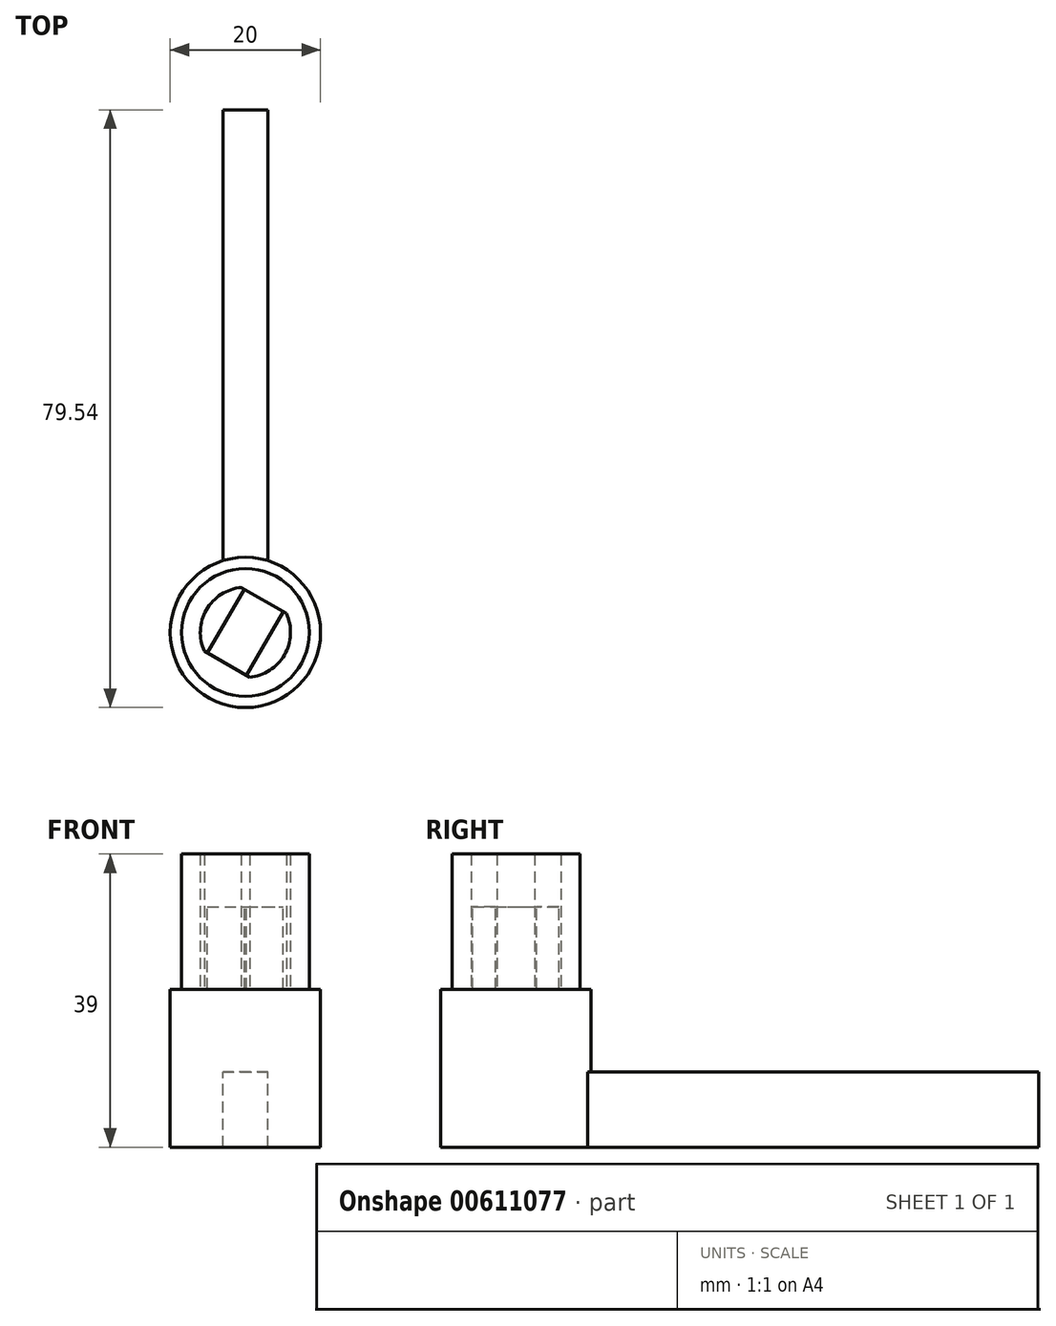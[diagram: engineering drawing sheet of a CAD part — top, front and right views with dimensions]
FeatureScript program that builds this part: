
annotation { "Feature Type Name" : "Feature", "Feature Type Description" : "" }
export const myFeature = defineFeature(function(context is Context, id is Id, definition is map)
    precondition{}
    {
        {
            var Q0;
            Q0=qCreatedBy(makeId("Top.planeOp"),FACE);
            var sketch = newSketch(context, id + "F0", { "sketchPlane" : qUnion([Q0])});
            skCircle(sketch, "E0", {"center": v(0, 0) * mm, "radius": 8.5 * mm});
            skArc(sketch, "E1", {"start": v(-0.55, 5.97) * mm, "mid": v(-5.2, 3) * mm, "end": v(-5.45, -2.51) * mm});
            skLineSegment(sketch, "E2.bottom", {"start": v(-0.55, 5.97) * mm, "end": v(5.45, 2.51) * mm});
            skLineSegment(sketch, "E2.top", {"start": v(-5.45, -2.51) * mm, "end": v(0.55, -5.97) * mm});
            skLineSegment(sketch, "E2.left", {"start": v(-0.55, 5.97) * mm, "end": v(-5.45, -2.51) * mm, "construction": true});
            skLineSegment(sketch, "E2.right", {"start": v(5.45, 2.51) * mm, "end": v(0.55, -5.97) * mm, "construction": true});
            skLineSegment(sketch, "E3", {"start": v(0, 0) * mm, "end": v(0, -6) * mm, "construction": true});
            skArc(sketch, "E4.trimOffspring", {"start": v(0.55, -5.97) * mm, "mid": v(5.2, -3) * mm, "end": v(5.45, 2.51) * mm});
            skSolve(sketch);
        }
        {
            var Q0;
            Q0=makeQuery(id+"F0.imprint","IMPRINT",FACE,{"disambiguationData":[TD([[makeQuery(id+"F0.imprint","IMPRINT",EDGE,{"derivedFrom":sQuery(id+"F0.wireOp",EDGE,"E0")}),1.0]])]});
            extrude(context, id + "F1", {"entities" : qUnion([Q0]), "depth" : 18 * mm, "offsetDistance" : 25 * mm});
        }
        {
            var Q0;
            Q0=qCreatedBy(makeId("Top.planeOp"),FACE);
            var sketch = newSketch(context, id + "F2", { "sketchPlane" : qUnion([Q0])});
            skLineSegment(sketch, "E5.bottom", {"start": v(-5.7, -3.88) * mm, "end": v(-0.5, -6.88) * mm});
            skLineSegment(sketch, "E5.top", {"start": v(0.5, 6.88) * mm, "end": v(5.7, 3.88) * mm});
            skLineSegment(sketch, "E5.left", {"start": v(-5.7, -3.88) * mm, "end": v(0.5, 6.88) * mm});
            skLineSegment(sketch, "E5.right", {"start": v(-0.5, -6.88) * mm, "end": v(5.7, 3.88) * mm});
            skPoint(sketch, "E5.middle", {"position": v(0, 0) * mm});
            skLineSegment(sketch, "E6", {"start": v(0, 0) * mm, "end": v(0, -8.5) * mm});
            skSolve(sketch);
        }
        {
            var Q0;
            Q0 = qSketchRegion(id + "F2", true);
            extrude(context, id + "F3", {"entities" : qUnion([Q0]), "operationType" : NewBodyOperationType.ADD, "depth" : 11 * mm, "offsetDistance" : 25 * mm});
        }
        {
            var Q0;
            Q0=qCreatedBy(makeId("Top.planeOp"),FACE);
            var sketch = newSketch(context, id + "F4", { "sketchPlane" : qUnion([Q0])});
            skCircle(sketch, "E7", {"center": v(0, 0) * mm, "radius": 10 * mm});
            skSolve(sketch);
        }
        {
            var Q0;
            Q0 = qSketchRegion(id + "F4", true);
            extrude(context, id + "F5", {"entities" : qUnion([Q0]), "operationType" : NewBodyOperationType.ADD, "oppositeDirection" : true, "depth" : 11 * mm, "offsetDistance" : 25 * mm});
        }
        {
            var Q0;
            Q0=makeQuery(id+"F5.opExtrude","CAP_FACE",FACE,{"disambiguationData":[OSD([sQuery(id+"F4.wireOp",EDGE,"E7")])],"isStart":false});
            var sketch = newSketch(context, id + "F6", { "sketchPlane" : qUnion([Q0])});
            skArc(sketch, "E8", {"start": v(3, -9.54) * mm, "mid": v(0, 10) * mm, "end": v(-3, -9.54) * mm});
            skLineSegment(sketch, "E9.bottom", {"start": v(-3, -9.54) * mm, "end": v(3, -9.54) * mm, "construction": true});
            skLineSegment(sketch, "E9.top", {"start": v(-3, -69.54) * mm, "end": v(3, -69.54) * mm});
            skLineSegment(sketch, "E9.left", {"start": v(-3, -9.54) * mm, "end": v(-3, -69.54) * mm});
            skLineSegment(sketch, "E9.right", {"start": v(3, -9.54) * mm, "end": v(3, -69.54) * mm});
            skLineSegment(sketch, "E10", {"start": v(0, 0) * mm, "end": v(0, -9.54) * mm, "construction": true});
            skSolve(sketch);
        }
        {
            var Q0;
            Q0 = qSketchRegion(id + "F6", true);
            extrude(context, id + "F7", {"entities" : qUnion([Q0]), "operationType" : NewBodyOperationType.ADD, "depth" : 10 * mm, "offsetDistance" : 25 * mm});
        }
    });
